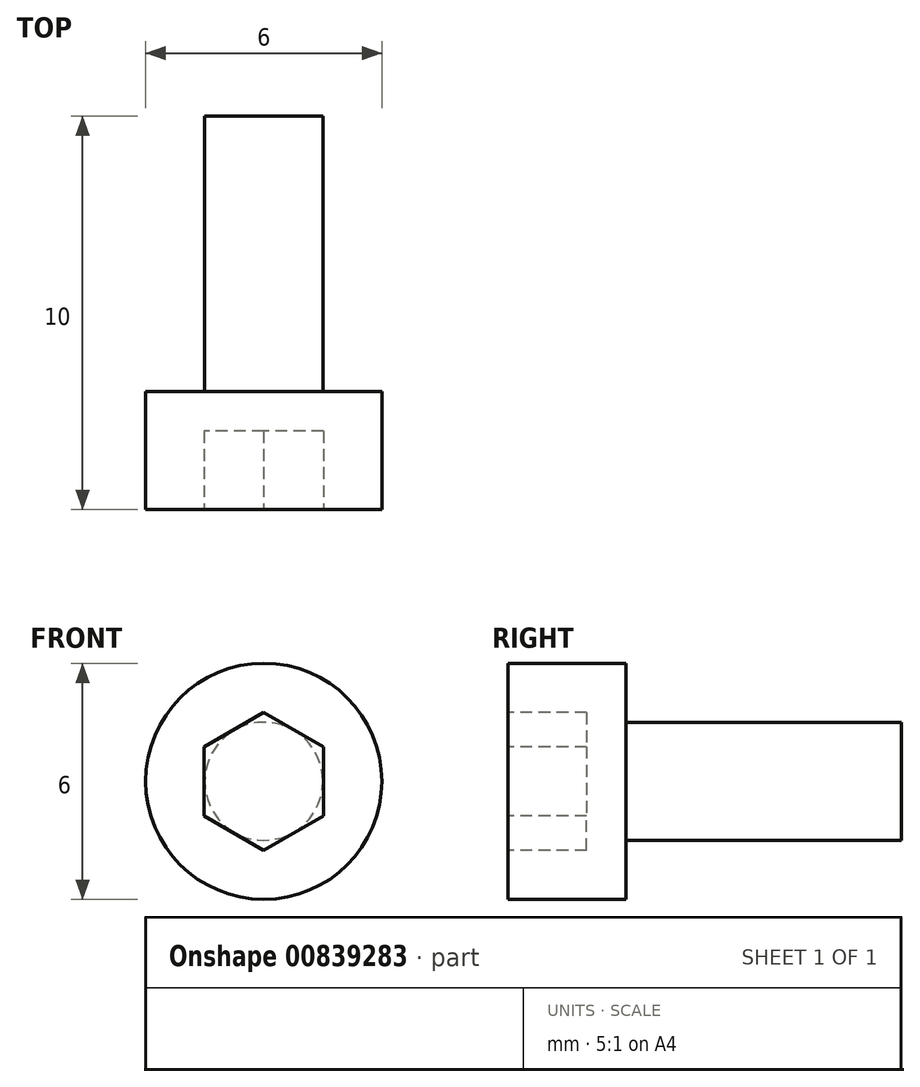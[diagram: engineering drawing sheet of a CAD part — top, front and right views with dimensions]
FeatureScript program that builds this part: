
annotation { "Feature Type Name" : "Feature", "Feature Type Description" : "" }
export const myFeature = defineFeature(function(context is Context, id is Id, definition is map)
    precondition{}
    {
        {
            var Q0;
            Q0=qCreatedBy(makeId("Front.planeOp"),FACE);
            var sketch = newSketch(context, id + "F0", { "sketchPlane" : qUnion([Q0])});
            skCircle(sketch, "E0", {"center": v(0, 0) * mm, "radius": 1.5 * mm});
            skSolve(sketch);
        }
        {
            var Q0;
            Q0=makeQuery(id+"F0.imprint","IMPRINT",FACE,{"disambiguationData":[TD([[makeQuery(id+"F0.imprint","IMPRINT",EDGE,{"derivedFrom":sQuery(id+"F0.wireOp",EDGE,"E0")}),1.0]])]});
            extrude(context, id + "F1", {"entities" : qUnion([Q0]), "oppositeDirection" : true, "depth" : 10 * mm, "offsetDistance" : 25 * mm});
        }
        {
            var Q0;
            Q0=makeQuery(id+"F1.opExtrude","CAP_FACE",FACE,{"disambiguationData":[OSD([sQuery(id+"F0.wireOp",EDGE,"E0")])],"isStart":true});
            var sketch = newSketch(context, id + "F2", { "sketchPlane" : qUnion([Q0])});
            skCircle(sketch, "E1.cCircle", {"center": v(0, 0) * mm, "radius": 2.75 * mm, "construction": true});
            skLineSegment(sketch, "E1.0", {"start": v(2.75, 0) * mm, "end": v(1.38, -2.38) * mm});
            skLineSegment(sketch, "E1.1", {"start": v(1.38, -2.38) * mm, "end": v(-1.37, -2.38) * mm});
            skLineSegment(sketch, "E1.2", {"start": v(-1.37, -2.38) * mm, "end": v(-2.75, 0) * mm});
            skLineSegment(sketch, "E1.3", {"start": v(-2.75, 0) * mm, "end": v(-1.38, 2.38) * mm});
            skLineSegment(sketch, "E1.4", {"start": v(-1.38, 2.38) * mm, "end": v(1.38, 2.38) * mm});
            skLineSegment(sketch, "E1.5", {"start": v(1.37, 2.38) * mm, "end": v(2.75, 0) * mm});
            skCircle(sketch, "E2", {"center": v(0, 0) * mm, "radius": 3 * mm});
            skSolve(sketch);
        }
        {
            var Q0;
            {var subQ0=sQuery(id+"F2.wireOp",EDGE,"E1.1");Q0=makeQuery(id+"F2.imprint","IMPRINT",FACE,{"disambiguationData":[TD([[makeQuery(id+"F2.imprint","IMPRINT",EDGE,{"derivedFrom":subQ0}),1.0]])]});}
            var Q1;
            {var subQ0=sQuery(id+"F2.wireOp",EDGE,"E1.0");Q1=makeQuery(id+"F2.imprint","IMPRINT",FACE,{"disambiguationData":[TD([[makeQuery(id+"F2.imprint","IMPRINT",EDGE,{"derivedFrom":subQ0}),1.0]])]});}
            var Q2;
            Q2=makeQuery(id+"F2.imprint","IMPRINT",FACE,{"disambiguationData":[TD([[makeQuery(id+"F2.imprint","IMPRINT",EDGE,{"derivedFrom":sQuery(id+"F2.wireOp",EDGE,"E1.0")}),-1.0]])]});
            var Q3;
            {var subQ0=sQuery(id+"F2.wireOp",EDGE,"E1.5");Q3=makeQuery(id+"F2.imprint","IMPRINT",FACE,{"disambiguationData":[TD([[makeQuery(id+"F2.imprint","IMPRINT",EDGE,{"derivedFrom":subQ0}),1.0]])]});}
            var Q4;
            {var subQ0=sQuery(id+"F2.wireOp",EDGE,"E1.4");Q4=makeQuery(id+"F2.imprint","IMPRINT",FACE,{"disambiguationData":[TD([[makeQuery(id+"F2.imprint","IMPRINT",EDGE,{"derivedFrom":subQ0}),1.0]])]});}
            var Q5;
            {var subQ0=sQuery(id+"F2.wireOp",EDGE,"E1.3");Q5=makeQuery(id+"F2.imprint","IMPRINT",FACE,{"disambiguationData":[TD([[makeQuery(id+"F2.imprint","IMPRINT",EDGE,{"derivedFrom":subQ0}),1.0]])]});}
            var Q6;
            {var subQ0=sQuery(id+"F2.wireOp",EDGE,"E1.2");Q6=makeQuery(id+"F2.imprint","IMPRINT",FACE,{"disambiguationData":[TD([[makeQuery(id+"F2.imprint","IMPRINT",EDGE,{"derivedFrom":subQ0}),1.0]])]});}
            extrude(context, id + "F3", {"entities" : qUnion([Q0, Q1, Q2, Q3, Q4, Q5, Q6]), "operationType" : NewBodyOperationType.ADD, "oppositeDirection" : true, "depth" : 3 * mm, "offsetDistance" : 25 * mm});
        }
        {
            var Q0;
            Q0=makeQuery(id+"F2.imprint","IMPRINT",FACE,{"disambiguationData":[TD([[makeQuery(id+"F2.imprint","IMPRINT",EDGE,{"derivedFrom":sQuery(id+"F2.wireOp",EDGE,"E1.0")}),-1.0]])]});
            var sketch = newSketch(context, id + "F4", { "sketchPlane" : qUnion([Q0])});
            skCircle(sketch, "E3.cCircle", {"center": v(0, 0) * mm, "radius": 1.75 * mm, "construction": true});
            skLineSegment(sketch, "E3.0", {"start": v(0, -1.75) * mm, "end": v(-1.52, -0.87) * mm});
            skLineSegment(sketch, "E3.1", {"start": v(-1.52, -0.88) * mm, "end": v(-1.52, 0.87) * mm});
            skLineSegment(sketch, "E3.2", {"start": v(-1.52, 0.87) * mm, "end": v(0, 1.75) * mm});
            skLineSegment(sketch, "E3.3", {"start": v(0, 1.75) * mm, "end": v(1.52, 0.88) * mm});
            skLineSegment(sketch, "E3.4", {"start": v(1.52, 0.88) * mm, "end": v(1.52, -0.87) * mm});
            skLineSegment(sketch, "E3.5", {"start": v(1.52, -0.87) * mm, "end": v(0, -1.75) * mm});
            skSolve(sketch);
        }
        {
            var Q0;
            Q0=makeQuery(id+"F4.imprint","IMPRINT",FACE,{"disambiguationData":[TD([[makeQuery(id+"F4.imprint","IMPRINT",EDGE,{"derivedFrom":sQuery(id+"F4.wireOp",EDGE,"E3.0")}),-1.0]])]});
            var Q1;
            Q1=makeQuery(id+"F4.imprint","IMPRINT",FACE,{"disambiguationData":[TD([[makeQuery(id+"F4.imprint","IMPRINT",EDGE,{"derivedFrom":makeQuery(id+"F2.imprint","IMPRINT",EDGE,{"derivedFrom":makeQuery(id+"F1.opExtrude","CAP_EDGE",EDGE,{"disambiguationData":[OSD([sQuery(id+"F0.wireOp",EDGE,"E0")])],"isStart":true})})}),1.0]])]});
            extrude(context, id + "F5", {"entities" : qUnion([Q0, Q1]), "operationType" : NewBodyOperationType.REMOVE, "oppositeDirection" : true, "depth" : 2 * mm, "offsetDistance" : 25 * mm});
        }
    });
